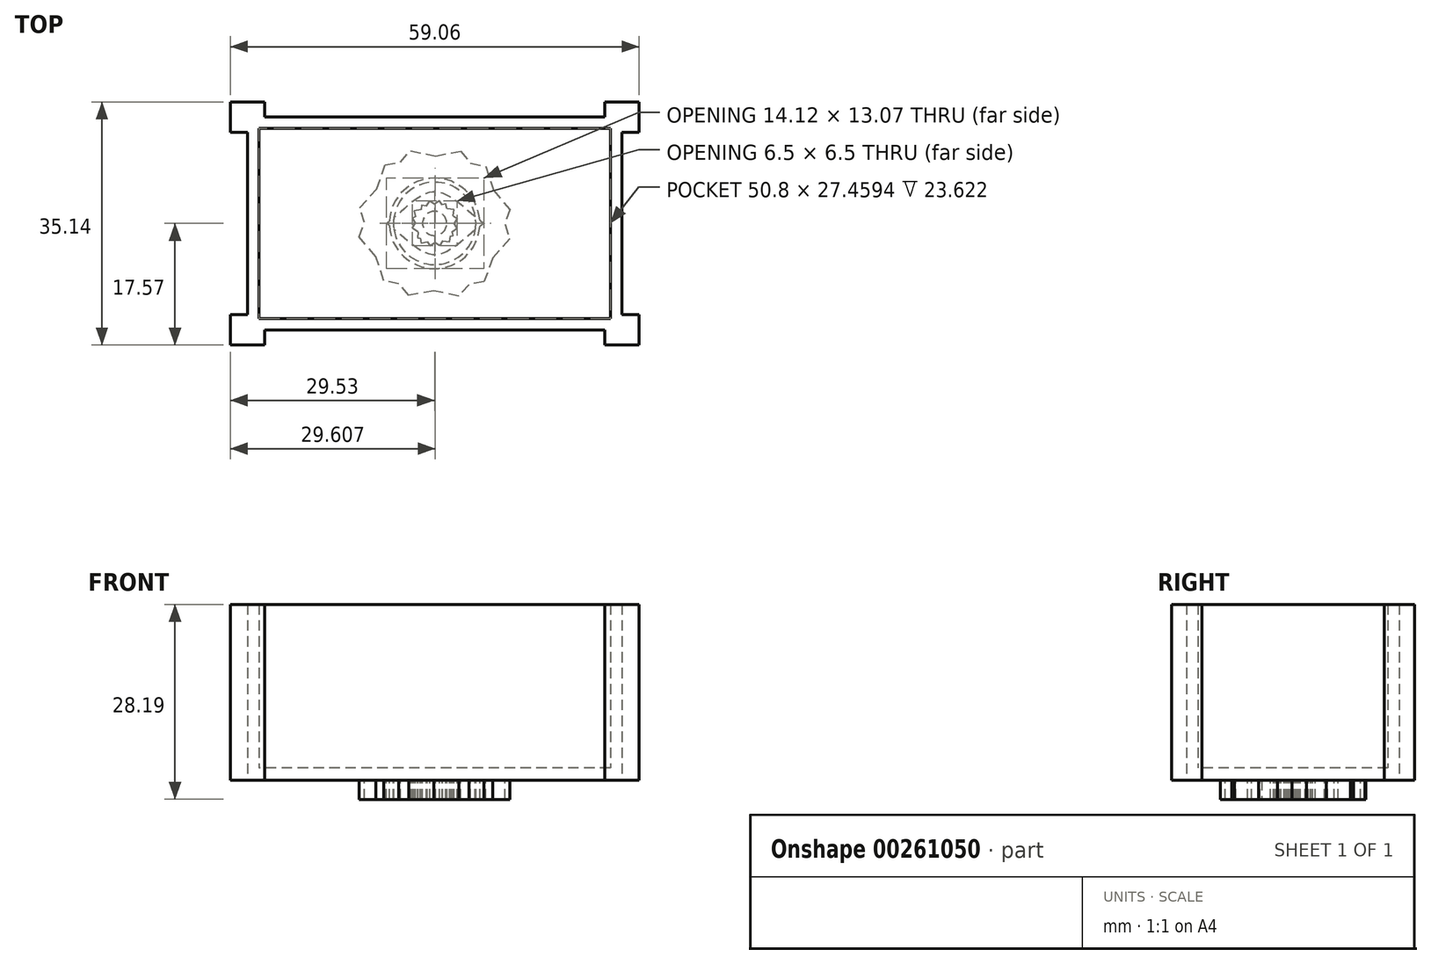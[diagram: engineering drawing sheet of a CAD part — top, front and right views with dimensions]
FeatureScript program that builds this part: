
annotation { "Feature Type Name" : "Feature", "Feature Type Description" : "" }
export const myFeature = defineFeature(function(context is Context, id is Id, definition is map)
    precondition{}
    {
        {
            var Q0;
            Q0=qCreatedBy(makeId("Top.planeOp"),FACE);
            var sketch = newSketch(context, id + "F0", { "sketchPlane" : qUnion([Q0])});
            skLineSegment(sketch, "E0.bottom", {"start": v(27.05, 15.38) * mm, "end": v(-27.05, 15.38) * mm});
            skLineSegment(sketch, "E0.top", {"start": v(27.05, -15.38) * mm, "end": v(-27.05, -15.38) * mm});
            skLineSegment(sketch, "E0.left", {"start": v(27.05, 15.38) * mm, "end": v(27.05, -15.38) * mm});
            skLineSegment(sketch, "E0.right", {"start": v(-27.05, 15.38) * mm, "end": v(-27.05, -15.38) * mm});
            skPoint(sketch, "E0.middle", {"position": v(0, 0) * mm});
            skLineSegment(sketch, "E1.bottom", {"start": v(25.4, 13.73) * mm, "end": v(-25.4, 13.73) * mm});
            skLineSegment(sketch, "E1.top", {"start": v(25.4, -13.73) * mm, "end": v(-25.4, -13.73) * mm});
            skLineSegment(sketch, "E1.left", {"start": v(25.4, 13.73) * mm, "end": v(25.4, -13.73) * mm});
            skLineSegment(sketch, "E1.right", {"start": v(-25.4, 13.73) * mm, "end": v(-25.4, -13.73) * mm});
            skLineSegment(sketch, "E2.bottom", {"start": v(-29.53, 17.57) * mm, "end": v(-24.57, 17.57) * mm});
            skLineSegment(sketch, "E2.top", {"start": v(-29.53, 13.2) * mm, "end": v(-27.05, 13.2) * mm});
            skLineSegment(sketch, "E2.left", {"start": v(-29.53, 17.57) * mm, "end": v(-29.53, 13.2) * mm});
            skLineSegment(sketch, "E2.right", {"start": v(-24.57, 17.57) * mm, "end": v(-24.57, 15.38) * mm});
            skPoint(sketch, "E2.middle", {"position": v(-27.05, 15.38) * mm});
            skLineSegment(sketch, "E3.MirrorCS", {"start": v(29.53, 17.57) * mm, "end": v(24.57, 17.57) * mm});
            skLineSegment(sketch, "E4.MirrorCS", {"start": v(29.53, 17.57) * mm, "end": v(29.53, 13.2) * mm});
            skLineSegment(sketch, "E5.MirrorCS", {"start": v(29.53, 13.2) * mm, "end": v(27.05, 13.2) * mm});
            skLineSegment(sketch, "E6.MirrorCS", {"start": v(24.57, 17.57) * mm, "end": v(24.57, 15.38) * mm});
            skLineSegment(sketch, "E7.MirrorCS", {"start": v(-29.53, -13.2) * mm, "end": v(-27.05, -13.2) * mm});
            skLineSegment(sketch, "E8.MirrorCS", {"start": v(-29.53, -17.57) * mm, "end": v(-24.57, -17.57) * mm});
            skLineSegment(sketch, "E9.MirrorCS", {"start": v(-29.53, -17.57) * mm, "end": v(-29.53, -13.2) * mm});
            skLineSegment(sketch, "E10.MirrorCS", {"start": v(-24.57, -17.57) * mm, "end": v(-24.57, -15.38) * mm});
            skLineSegment(sketch, "E11.MirrorCS", {"start": v(29.53, -13.2) * mm, "end": v(27.05, -13.2) * mm});
            skLineSegment(sketch, "E12.MirrorCS", {"start": v(29.53, -17.57) * mm, "end": v(29.53, -13.2) * mm});
            skLineSegment(sketch, "E13.MirrorCS", {"start": v(29.53, -17.57) * mm, "end": v(24.57, -17.57) * mm});
            skLineSegment(sketch, "E14.MirrorCS", {"start": v(24.57, -17.57) * mm, "end": v(24.57, -15.38) * mm});
            skPoint(sketch, "E15.orphan", {"position": v(-24.57, 13.2) * mm});
            skPoint(sketch, "E16.orphan", {"position": v(24.57, 13.2) * mm});
            skPoint(sketch, "E17.orphan", {"position": v(24.57, -13.2) * mm});
            skPoint(sketch, "E18.orphan", {"position": v(-24.57, -13.2) * mm});
            skSolve(sketch);
        }
        {
            var Q0;
            Q0=makeQuery(id+"F0.imprint","IMPRINT",FACE,{"disambiguationData":[TD([[makeQuery(id+"F0.imprint","IMPRINT",EDGE,{"derivedFrom":sQuery(id+"F0.wireOp",EDGE,"E0.bottom")}),1.0]])]});
            extrude(context, id + "F1", {"entities" : qUnion([Q0]), "depth" : 25.4 * mm});
        }
        {
            var Q0;
            Q0=makeQuery(id+"F0.imprint","IMPRINT",FACE,{"disambiguationData":[TD([[makeQuery(id+"F0.imprint","IMPRINT",EDGE,{"derivedFrom":sQuery(id+"F0.wireOp",EDGE,"E1.bottom")}),1.0]])]});
            extrude(context, id + "F2", {"entities" : qUnion([Q0]), "operationType" : NewBodyOperationType.ADD, "depth" : 1.78 * mm});
        }
        {
            var Q0;
            Q0 = qSketchRegion(id + "F0", true);
            extrude(context, id + "F3", {"entities" : qUnion([Q0]), "operationType" : NewBodyOperationType.ADD, "depth" : 25.4 * mm});
        }
        {
            var Q0;
            Q0=makeQuery(id+"F0.imprint","IMPRINT",FACE,{"disambiguationData":[TD([[makeQuery(id+"F0.imprint","IMPRINT",EDGE,{"derivedFrom":sQuery(id+"F0.wireOp",EDGE,"E1.bottom")}),1.0]])]});
            var sketch = newSketch(context, id + "F4", { "sketchPlane" : qUnion([Q0])});
            skLineSegment(sketch, "E19.0", {"start": v(7.15, -8.45) * mm, "end": v(4.97, -8.84) * mm});
            skLineSegment(sketch, "E19.1", {"start": v(-3.74, -10.42) * mm, "end": v(-5.17, -8.72) * mm});
            skLineSegment(sketch, "E19.2", {"start": v(-10.9, -1.97) * mm, "end": v(-10.14, 0.12) * mm});
            skLineSegment(sketch, "E19.3", {"start": v(-7.15, 8.45) * mm, "end": v(-4.97, 8.84) * mm});
            skLineSegment(sketch, "E19.4", {"start": v(3.74, 10.42) * mm, "end": v(5.17, 8.72) * mm});
            skLineSegment(sketch, "E19.5", {"start": v(10.9, 1.97) * mm, "end": v(10.14, -0.12) * mm});
            skPoint(sketch, "E19.0.midPoint", {"position": v(1.7, -9.43) * mm});
            skLineSegment(sketch, "E20.0", {"start": v(10.84, -2.23) * mm, "end": v(8.4, -4.98) * mm});
            skLineSegment(sketch, "E20.1", {"start": v(3.5, -10.5) * mm, "end": v(-0.11, -9.76) * mm});
            skLineSegment(sketch, "E20.2", {"start": v(-7.35, -8.28) * mm, "end": v(-8.51, -4.78) * mm});
            skLineSegment(sketch, "E20.3", {"start": v(-10.84, 2.23) * mm, "end": v(-8.4, 4.98) * mm});
            skLineSegment(sketch, "E20.4", {"start": v(-3.5, 10.5) * mm, "end": v(0.11, 9.76) * mm});
            skLineSegment(sketch, "E20.5", {"start": v(7.35, 8.28) * mm, "end": v(8.51, 4.78) * mm});
            skPoint(sketch, "E20.0.midPoint", {"position": v(7.17, -6.37) * mm});
            skCircle(sketch, "E21", {"center": v(0, 0) * mm, "radius": 6.54 * mm});
            skCircle(sketch, "E22", {"center": v(0, 0) * mm, "radius": 5.96 * mm});
            skPoint(sketch, "E23", {"position": v(-9.1, -3.02) * mm});
            skFitSpline(sketch, "E24", {"points": [v(7.14, 0) * mm, v(0, -4.55) * mm, v(-6.98, 0) * mm], "startDerivative": vector(-14.25, -9.56) * mm, "endDerivative": vector(-13.98, 9.6) * mm});
            skFitSpline(sketch, "E25.MirrorCS", {"points": [v(7.14, 0) * mm, v(0, 4.55) * mm, v(-6.98, 0) * mm], "startDerivative": vector(-14.25, 9.56) * mm, "endDerivative": vector(-13.98, -9.6) * mm});
            skLineSegment(sketch, "E26.0", {"start": v(3.25, 0.7) * mm, "end": v(2.8, 0) * mm});
            skLineSegment(sketch, "E26.1", {"start": v(0.7, -3.25) * mm, "end": v(0, -2.8) * mm});
            skLineSegment(sketch, "E26.2", {"start": v(-3.25, -0.7) * mm, "end": v(-2.8, 0) * mm});
            skLineSegment(sketch, "E26.3", {"start": v(-0.7, 3.25) * mm, "end": v(0, 2.8) * mm});
            skPoint(sketch, "E26.0.midPoint", {"position": v(1.97, -1.28) * mm});
            skLineSegment(sketch, "E27.MirrorCS", {"start": v(-0.7, -3.25) * mm, "end": v(0, -2.8) * mm});
            skLineSegment(sketch, "E28.MirrorCS", {"start": v(3.25, -0.7) * mm, "end": v(2.8, 0) * mm});
            skLineSegment(sketch, "E29.MirrorCS", {"start": v(-3.25, 0.7) * mm, "end": v(-2.8, 0) * mm});
            skLineSegment(sketch, "E30.MirrorCS", {"start": v(0.7, 3.25) * mm, "end": v(0, 2.8) * mm});
            skLineSegment(sketch, "E31.MirrorCS", {"start": v(-1.93, -2.82) * mm, "end": v(-1.1, -2.63) * mm});
            skLineSegment(sketch, "E32.MirrorCS", {"start": v(2.65, -1.77) * mm, "end": v(2.52, -1.17) * mm});
            skLineSegment(sketch, "E33.MirrorCS", {"start": v(-2.98, 1.77) * mm, "end": v(-2.8, 0.99) * mm});
            skLineSegment(sketch, "E34.MirrorCS", {"start": v(1.6, 2.82) * mm, "end": v(1.06, 2.7) * mm});
            skLineSegment(sketch, "E35.MirrorCS", {"start": v(-2.48, -2.07) * mm, "end": v(-2.09, -2.12) * mm});
            skLineSegment(sketch, "E36.MirrorCS", {"start": v(2.19, -2.65) * mm, "end": v(2.29, -1.85) * mm});
            skLineSegment(sketch, "E37.MirrorCS", {"start": v(-1.9, 2.6) * mm, "end": v(-1.97, 2) * mm});
            skLineSegment(sketch, "E38.MirrorCS", {"start": v(2.77, 2.01) * mm, "end": v(1.76, 2.14) * mm});
            skCircle(sketch, "E39", {"center": v(0, 0) * mm, "radius": 1.75 * mm});
            skLineSegment(sketch, "E40.trimOffspring", {"start": v(-8.51, -4.78) * mm, "end": v(-10.9, -1.97) * mm});
            skLineSegment(sketch, "E41.trimOffspring", {"start": v(-5.17, -8.72) * mm, "end": v(-7.35, -8.28) * mm});
            skLineSegment(sketch, "E42.trimOffspring", {"start": v(-0.11, -9.76) * mm, "end": v(-3.74, -10.42) * mm});
            skLineSegment(sketch, "E43.trimOffspring", {"start": v(4.97, -8.84) * mm, "end": v(3.5, -10.5) * mm});
            skLineSegment(sketch, "E44.trimOffspring", {"start": v(8.4, -4.98) * mm, "end": v(7.15, -8.45) * mm});
            skLineSegment(sketch, "E45.trimOffspring", {"start": v(10.14, -0.12) * mm, "end": v(10.84, -2.23) * mm});
            skLineSegment(sketch, "E46.trimOffspring", {"start": v(8.51, 4.78) * mm, "end": v(10.9, 1.97) * mm});
            skLineSegment(sketch, "E47.trimOffspring", {"start": v(5.17, 8.72) * mm, "end": v(7.35, 8.28) * mm});
            skLineSegment(sketch, "E48.trimOffspring", {"start": v(0.11, 9.76) * mm, "end": v(3.74, 10.42) * mm});
            skLineSegment(sketch, "E49.trimOffspring", {"start": v(-4.97, 8.84) * mm, "end": v(-3.5, 10.5) * mm});
            skLineSegment(sketch, "E50.trimOffspring", {"start": v(-8.4, 4.98) * mm, "end": v(-7.15, 8.45) * mm});
            skLineSegment(sketch, "E51.trimOffspring", {"start": v(-10.14, 0.12) * mm, "end": v(-10.84, 2.23) * mm});
            skLineSegment(sketch, "E52.trimOffspring", {"start": v(1.17, -2.52) * mm, "end": v(2.19, -2.65) * mm});
            skLineSegment(sketch, "E53.trimOffspring", {"start": v(-2.37, -1.26) * mm, "end": v(-3.25, -0.7) * mm});
            skLineSegment(sketch, "E54.trimOffspring", {"start": v(-1.1, -2.63) * mm, "end": v(-0.7, -3.25) * mm});
            skLineSegment(sketch, "E55.trimOffspring", {"start": v(2.29, -1.85) * mm, "end": v(2.65, -1.77) * mm});
            skLineSegment(sketch, "E56.trimOffspring", {"start": v(2.52, -1.17) * mm, "end": v(3.25, -0.7) * mm});
            skLineSegment(sketch, "E57.trimOffspring", {"start": v(-2.09, -2.12) * mm, "end": v(-1.93, -2.82) * mm});
            skLineSegment(sketch, "E58.trimOffspring", {"start": v(-2.37, -1.26) * mm, "end": v(-2.48, -2.07) * mm});
            skLineSegment(sketch, "E59.trimOffspring", {"start": v(1.17, -2.52) * mm, "end": v(0.7, -3.25) * mm});
            skLineSegment(sketch, "E60.trimOffspring", {"start": v(-1.18, 2.5) * mm, "end": v(-0.7, 3.25) * mm});
            skLineSegment(sketch, "E61.trimOffspring", {"start": v(-2.8, 0.99) * mm, "end": v(-3.25, 0.7) * mm});
            skLineSegment(sketch, "E62.trimOffspring", {"start": v(-1.97, 2) * mm, "end": v(-2.98, 1.77) * mm});
            skLineSegment(sketch, "E63.trimOffspring", {"start": v(-1.18, 2.5) * mm, "end": v(-1.9, 2.6) * mm});
            skLineSegment(sketch, "E64.trimOffspring", {"start": v(1.06, 2.7) * mm, "end": v(0.7, 3.25) * mm});
            skLineSegment(sketch, "E65.trimOffspring", {"start": v(1.76, 2.14) * mm, "end": v(1.6, 2.82) * mm});
            skLineSegment(sketch, "E66.trimOffspring", {"start": v(2.65, 1.08) * mm, "end": v(3.25, 0.7) * mm});
            skLineSegment(sketch, "E67.trimOffspring", {"start": v(2.65, 1.08) * mm, "end": v(2.77, 2.01) * mm});
            skSolve(sketch);
        }
        {
            var Q0;
            Q0=makeQuery(id+"F4.imprint","IMPRINT",FACE,{"disambiguationData":[TD([[makeQuery(id+"F4.imprint","IMPRINT",EDGE,{"derivedFrom":sQuery(id+"F4.wireOp",EDGE,"E19.0")}),-1.0]])]});
            var Q1;
            {var subQ0=sQuery(id+"F4.wireOp",EDGE,"E24");var subQ1=sQuery(id+"F4.wireOp",EDGE,"E22");var subQ2=makeQuery(id+"F4.imprint","INTERSECT",VERTEX,{"disambiguationData":[OD(0.0)],"derivedFrom":[subQ1,subQ0]});Q1=makeQuery(id+"F4.imprint","IMPRINT",FACE,{"disambiguationData":[TD([[makeQuery(id+"F4.imprint","IMPRINT",EDGE,{"disambiguationData":[TD([[subQ2,-1.0]])],"derivedFrom":subQ1}),1.0]])]});}
            var Q2;
            {var subQ0=sQuery(id+"F4.wireOp",EDGE,"E25.MirrorCS");var subQ1=sQuery(id+"F4.wireOp",EDGE,"E22");var subQ2=makeQuery(id+"F4.imprint","INTERSECT",VERTEX,{"disambiguationData":[OD(0.0)],"derivedFrom":[subQ1,subQ0]});Q2=makeQuery(id+"F4.imprint","IMPRINT",FACE,{"disambiguationData":[TD([[makeQuery(id+"F4.imprint","IMPRINT",EDGE,{"disambiguationData":[TD([[subQ2,1.0]])],"derivedFrom":subQ1}),1.0]])]});}
            var Q3;
            Q3=makeQuery(id+"F4.imprint","IMPRINT",FACE,{"disambiguationData":[TD([[makeQuery(id+"F4.imprint","IMPRINT",EDGE,{"derivedFrom":sQuery(id+"F4.wireOp",EDGE,"E39")}),1.0]])]});
            extrude(context, id + "F5", {"entities" : qUnion([Q0, Q1, Q2, Q3]), "oppositeDirection" : true, "depth" : 2.8 * mm});
        }
        {
            var Q0;
            Q0=makeQuery(id+"F4.imprint","IMPRINT",FACE,{"disambiguationData":[TD([[makeQuery(id+"F4.imprint","IMPRINT",EDGE,{"derivedFrom":sQuery(id+"F4.wireOp",EDGE,"E26.0")}),1.0]])]});
            extrude(context, id + "F6", {"entities" : qUnion([Q0]), "oppositeDirection" : true, "depth" : 2.8 * mm});
        }
    });
